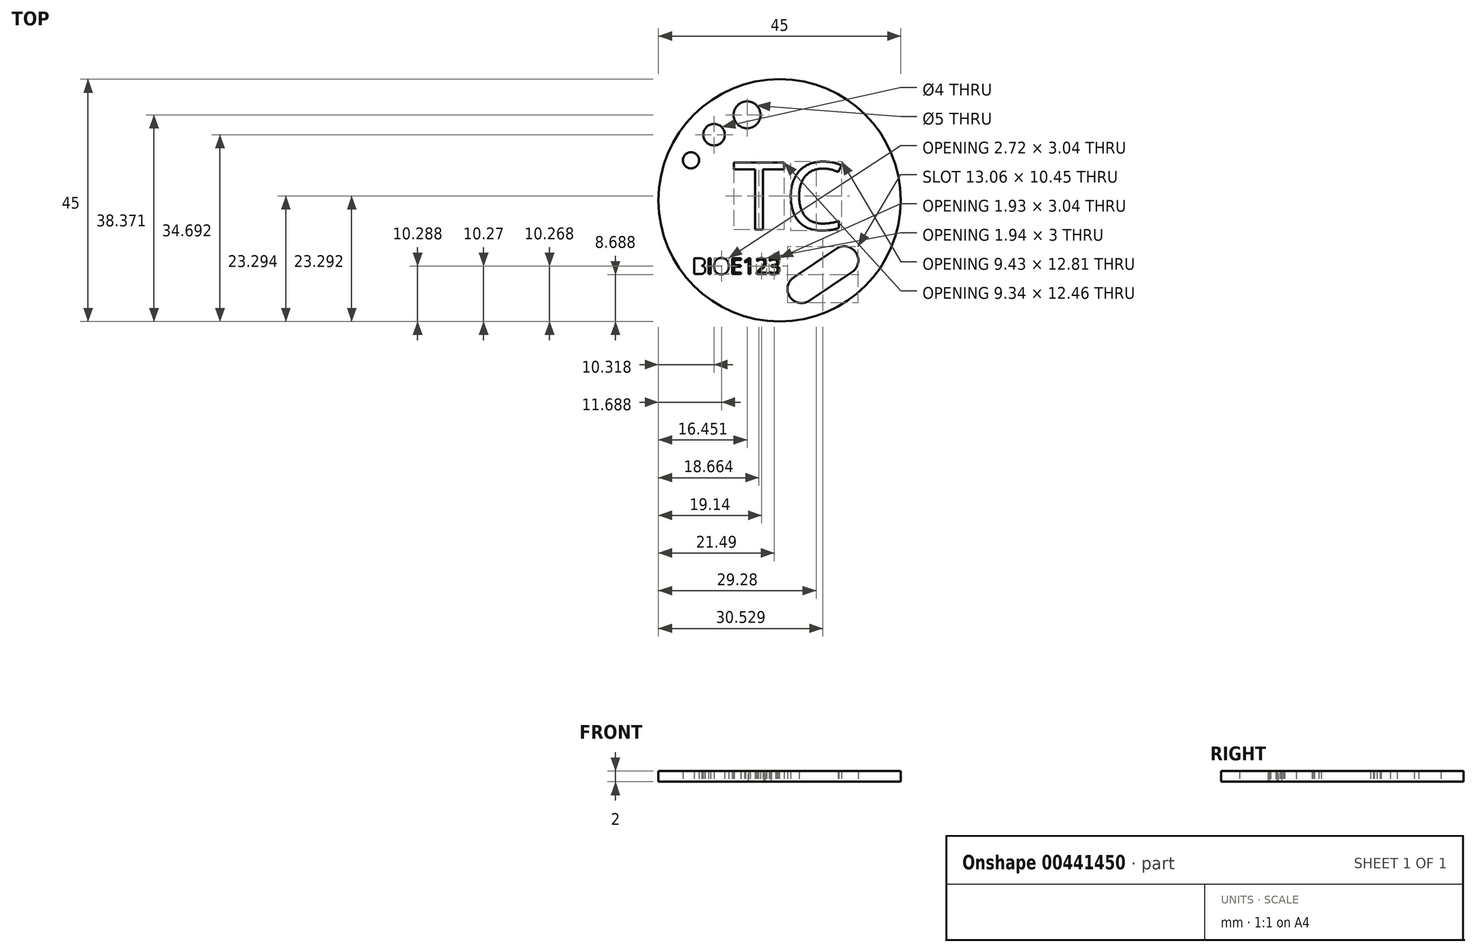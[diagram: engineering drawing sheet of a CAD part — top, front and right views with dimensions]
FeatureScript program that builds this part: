
annotation { "Feature Type Name" : "Feature", "Feature Type Description" : "" }
export const myFeature = defineFeature(function(context is Context, id is Id, definition is map)
    precondition{}
    {
        {
            var Q0;
            Q0=qCreatedBy(makeId("Top.planeOp"),FACE);
            var sketch = newSketch(context, id + "F0", { "sketchPlane" : qUnion([Q0])});
            skCircle(sketch, "E0", {"center": v(0, 0) * mm, "radius": 22.5 * mm});
            skCircle(sketch, "E1", {"center": v(-16.47, 7.44) * mm, "radius": 1.5 * mm});
            skCircle(sketch, "E2", {"center": v(-12.18, 12.2) * mm, "radius": 2 * mm});
            skCircle(sketch, "E3", {"center": v(-6.05, 15.87) * mm, "radius": 2.5 * mm});
            skText(sketch, "E4", { "text": "TC", "fontName": "OpenSans-Regular.ttf"});
            skCircle(sketch, "E5", {"center": v(4.06, -16.48) * mm, "radius": 2.6 * mm});
            skCircle(sketch, "E6", {"center": v(12, -11.15) * mm, "radius": 2.6 * mm});
            skLineSegment(sketch, "E7", {"start": v(2.6, -14.31) * mm, "end": v(10.54, -8.98) * mm});
            skLineSegment(sketch, "E8", {"start": v(5.51, -18.64) * mm, "end": v(13.45, -13.3) * mm});
            skText(sketch, "E9", { "text": "BIOE123\n", "fontName": "OpenSans-Regular.ttf"});
            const initialGuessF0  = {"E4": [-0.00866, -0.00544, 1, 0, 0.01257], "E9": [-0.01626, -0.01371, 1, 0, 0.00298]};
            skSetInitialGuess(sketch, initialGuessF0);
            skSolve(sketch);
        }
        {
            var Q0;
            Q0=makeQuery(id+"F0.imprint","IMPRINT",FACE,{"disambiguationData":[TD([[makeQuery(id+"F0.imprint","IMPRINT",EDGE,{"derivedFrom":sQuery(id+"F0.wireOp",EDGE,"E0")}),1.0]])]});
            extrude(context, id + "F1", {"entities" : qUnion([Q0]), "depth" : 2 * mm});
        }
    });
